# Revit family: Civil-Drainage-Channel-ACO-RoadDrain 200
name_source: partatom
category: Generic Models
revit_build: Autodesk Revit 2013 (Build: 20120221_2030(x64)
units: mm (PartAtom-declared; Revit-internal decimal feet)

## types (10) — shared parameters
Assembly Code = D2040
Fax = +44 (0)1462 815895
Installation guidelines = http://www.aco.co.uk
Maintenance guidelines = http://www.aco.co.uk
Manufacturer = ACO Technologies plc - ACO Water Management Division
Model = ACO RoadDrain 200 PD200F
Model Description = Monolithic Channel drainage system
Price = POA - contact ACO
Product Page URL = http://www.aco.co.uk
Product brochure = http://www.aco.co.uk
Revision = 1
SerialNumber = 0.000000
TagNumber = 0.000000
Telephone = +44 (0)1462 816666
URL = www.aco.co.uk
zero-valued in all types: Cost, Straight Void Start

## per-type parameters (varying)
- 33101 - PD200 F 10.1 Channel 500mm LG: ACO Hydraulic Design Software=http://www.acodesign.co.uk; Access unit=No; Channel 260mm Wide=Yes; Channel C.S.A=0.041m²; Channel Colour=Black; Channel Material=Vienite® Synthetic Resin Concrete; Channel Recyclable=Fully recyclable; Channel Recycled Material Content=20% minimum; Closing End Cap=No; Concrete Surround Volume - Load Class F 900 - Concrete Pavement=0.29m³/m; Hydraulic Performance=http://www.aco.co.uk; I/O End Cap Void=3000 mm  [stored 9.84252 ft]; Inlet Outlet end cap=No; Installation - Concrete Grade=Refer to brochure; Invert Depth=370mm; Invert Depth.=270 mm; Load Class=A 15 - F 900; Pipe Depth=6500 mm  [stored 21.3255 ft]; Product Code=33101; Product Dimensions=500mm x 260mm x 400mm (LxWxH); Product Standard=BS EN 1433:2002, CE marked, Kitemarked; Product Weight=52.0 Kg; Total Depth=400 mm  [stored 1.31234 ft]; Type Comments=ACO RoadDrain 200 PD200F 10.1 Constant Depth Channel 500mm Long; Void Depth=-400 mm  [stored -1.31234 ft]
- 33201 - PD200 F 20.1 Channel 500mm LG: ACO Hydraulic Design Software=http://www.acodesign.co.uk; Access unit=No; Channel 260mm Wide=Yes; Channel C.S.A=0.051m²; Channel Colour=Black; Channel Material=Vienite® Synthetic Resin Concrete; Channel Recyclable=Fully recyclable; Channel Recycled Material Content=20% minimum; Closing End Cap=No; Concrete Surround Volume - Load Class F 900 - Concrete Pavement=0.31m³/m; Hydraulic Performance=http://www.aco.co.uk; I/O End Cap Void=3005 mm  [stored 9.85892 ft]; Inlet Outlet end cap=No; Installation - Concrete Grade=Refer to brochure; Invert Depth=420mm; Invert Depth.=320 mm  [stored 1.04987 ft]; Load Class=A 15 - F 900; Pipe Depth=5400 mm  [stored 17.7165 ft]; Product Code=33201; Product Dimensions=500mm x 260mm x 450mm (LxWxH); Product Standard=BS EN 1433:2002, CE marked, Kitemarked; Product Weight=54.5 Kg; Total Depth=450 mm  [stored 1.47638 ft]; Type Comments=ACO RoadDrain 200 PD200F 20.1 Constant Depth Channel 500mm Long; Void Depth=-450 mm  [stored -1.47638 ft]
- 33301 - PD200 F 30.1 Channel 500mm LG: ACO Hydraulic Design Software=http://www.acodesign.co.uk; Access unit=No; Channel 260mm Wide=Yes; Channel C.S.A=0.061m²; Channel Colour=Black; Channel Material=Vienite® Synthetic Resin Concrete; Channel Recyclable=Fully recyclable; Channel Recycled Material Content=20% minimum; Closing End Cap=No; Concrete Surround Volume - Load Class F 900 - Concrete Pavement=0.33m³/m; Hydraulic Performance=http://www.aco.co.uk; I/O End Cap Void=3010 mm  [stored 9.87533 ft]; Inlet Outlet end cap=No; Installation - Concrete Grade=Refer to brochure; Invert Depth=470mm; Invert Depth.=370 mm  [stored 1.21391 ft]; Load Class=A 15 - F 900; Pipe Depth=5750 mm  [stored 18.8648 ft]; Product Code=33301; Product Dimensions=500mm x 260mm x 500mm (LxWxH); Product Standard=BS EN 1433:2002, CE marked, Kitemarked; Product Weight=58.3 Kg; Total Depth=500 mm  [stored 1.64042 ft]; Type Comments=ACO RoadDrain 100 PD200F 30.1 Constant Depth Channel 500mm Long; Void Depth=-500 mm  [stored -1.64042 ft]
- 33103 - PD 200 F 10.3 Rodding Access 500mm LG: ACO Hydraulic Design Software=http://www.acodesign.co.uk; Access Cover/Frame Colour=Black; Access Cover/Frame Finish=Water Based Paint Coating; Access Cover/Frame Material=Ductile Iron; Access Cover/Frame Recyclable=Fully recyclable; Access Cover/Frame Recycled Material Content=Between 40% - 90%; Access unit=Yes; Channel 260mm Wide=No; Channel C.S.A=0.41m²; Channel Colour=Black; Channel Material=Vienite® Synthetic Resin Concrete; Channel Recyclable=Fully recyclable; Channel Recycled Material Content=20% minimum; Closing End Cap=No; Concrete Surround Volume - Load Class F 900 - Concrete Pavement=0.29m³/m; Hydraulic Performance=http://www.aco.co.uk; I/O End Cap Void=3500 mm  [stored 11.4829 ft]; Inlet Outlet end cap=No; Installation - Concrete Grade=Refer to brochure; Invert Depth=370mm; Invert Depth.=270 mm; Load Class=A 15 - F 900; Pipe Depth=6000 mm  [stored 19.685 ft]; Product Code=33103; Product Dimensions=500mm x 260mm x 400mm (LxWxH); Product Standard=BS EN 1433:2002, CE marked, Kitemarked; Product Weight=53.5 Kg; Total Depth=400 mm  [stored 1.31234 ft]; Type Comments=ACO RoadDrain 200 PD200F 10.3 Constant Depth Access Channel 500mm Long; Void Depth=-400 mm  [stored -1.31234 ft]
- 33203 - PD200 F 20.3 Rodding Access 500mm LG: ACO Hydraulic Design Software=http://www.acodesign.co.uk; Access Cover/Frame Colour=Black; Access Cover/Frame Finish=Water Based Paint Coating; Access Cover/Frame Material=Ductile Iron; Access Cover/Frame Recyclable=Fully recyclable; Access Cover/Frame Recycled Material Content=Between 40% - 90%; Access unit=Yes; Channel 260mm Wide=No; Channel C.S.A=0.051m²; Channel Colour=Black; Channel Material=Vienite® Synthetic Resin Concrete; Channel Recyclable=Fully recyclable; Channel Recycled Material Content=20% minimum; Closing End Cap=No; Concrete Surround Volume - Load Class F 900 - Concrete Pavement=0.31m³/m; Hydraulic Performance=http://www.aco.co.uk; I/O End Cap Void=3260 mm  [stored 10.6955 ft]; Inlet Outlet end cap=No; Installation - Concrete Grade=Refer to brochure; Invert Depth=420mm; Invert Depth.=320 mm  [stored 1.04987 ft]; Load Class=A 15 - F 900; Pipe Depth=5800 mm  [stored 19.0289 ft]; Product Code=33203; Product Dimensions=500mm x 260mm x 450mm (LxWxH); Product Standard=BS EN 1433:2002, CE marked, Kitemarked; Product Weight=53.5 Kg; Total Depth=450 mm  [stored 1.47638 ft]; Type Comments=ACO RoadDrain 200 PD200F 20.3 Constant Depth Access Channel 500mm Long; Void Depth=-450 mm  [stored -1.47638 ft]
- 33306 - PD200 F 306 Closing endcap: Access unit=No; Channel 260mm Wide=No; Closing End Cap=Yes; End Cap Colour=Black; End Cap Material=Vienite® Synthetic Resin Concrete; End Cap Recyclable=Fully recyclable; End Cap Recycled Material Content=20% minimum; I/O End Cap Void=3650 mm  [stored 11.9751 ft]; Inlet Outlet end cap=No; Invert Depth.=275 mm; Pipe Depth=3000 mm  [stored 9.84252 ft]; Product Code=33306; Product Dimensions=25mm x 260mm x 500mm (LxWxH); Product Weight=4.6 Kg; Total Depth=500 mm  [stored 1.64042 ft]; Type Comments=ACO RoadDrain PD200 F 306 Closing End Cap; Void Depth=-500 mm  [stored -1.64042 ft]
- 33108 - PD200 F 108 Inlet/outlet endcap: Access unit=No; Channel 260mm Wide=No; Closing End Cap=No; Connection Pipe Colour=Brown; Connection Pipe Material=PVCu; Connection Pipe O.D=Ø160mm; End Cap Colour=Black; End Cap Material=Vienite® Synthetic Resin Concrete; End Cap Recyclable=Fully recyclable; End Cap Recycled Material Content=20% minimum; I/O End Cap Void=128 mm; Inlet Outlet end cap=Yes; Invert Depth.=270 mm; Pipe Depth=299 mm; Product Code=33108; Product Dimensions=25mm x 260mm x 400mm (LxWxH); Product Weight=4.3 Kg; Total Depth=400 mm  [stored 1.31234 ft]; Type Comments=ACO RoadDrain PD200 F 108 Inlet/Outlet End Cap; Void Depth=-400 mm  [stored -1.31234 ft]
- 33208 - PD200 F 208 Inlet/outlet endcap: Access unit=No; Channel 260mm Wide=No; Closing End Cap=No; Connection Pipe Colour=Brown; Connection Pipe Material=PVCu; Connection Pipe O.D=Ø160mm; End Cap Colour=Black; End Cap Material=Vienite® Synthetic Resin Concrete; End Cap Recyclable=Fully recyclable; End Cap Recycled Material Content=20% minimum; I/O End Cap Void=228 mm  [stored 0.748031 ft]; Inlet Outlet end cap=Yes; Invert Depth.=275 mm; Pipe Depth=349 mm; Product Code=33208; Product Dimensions=25mm x 260mm x 450mm (LxWxH); Product Weight=4.7 Kg; Total Depth=450 mm  [stored 1.47638 ft]; Type Comments=ACO RoadDrain PD200 F 208 Inlet/Outlet End Cap; Void Depth=-450 mm  [stored -1.47638 ft]
- 33303 - PD 200 F 30.3 Rodding Access 500mm LG: ACO Hydraulic Design Software=http://www.acodesign.co.uk; Access Cover/Frame Colour=Black; Access Cover/Frame Finish=Water Based Paint Coating; Access Cover/Frame Material=Ductile Iron; Access Cover/Frame Recyclable=Fully recyclable; Access Cover/Frame Recycled Material Content=Between 40% - 90%; Access unit=Yes; Channel 260mm Wide=No; Channel C.S.A=0.061m²; Channel Colour=Black; Channel Material=Vienite® Synthetic Resin Concrete; Channel Recyclable=Fully recyclable; Channel Recycled Material Content=20% minimum; Closing End Cap=No; Concrete Surround Volume - Load Class F 900 - Concrete Pavement=0.33m³/m; Hydraulic Performance=http://www.aco.co.uk; I/O End Cap Void=3500 mm  [stored 11.4829 ft]; Inlet Outlet end cap=No; Installation - Concrete Grade=Refer to brochure; Invert Depth=470mm; Invert Depth.=370 mm  [stored 1.21391 ft]; Load Class=A 15 - F 900; Pipe Depth=5650 mm  [stored 18.5367 ft]; Product Code=33303; Product Dimensions=500mm x 260mm x 500mm (LxWxH); Product Standard=BS EN 1433:2002, CE marked, Kitemarked; Product Weight=66.0 Kg; Total Depth=500 mm  [stored 1.64042 ft]; Type Comments=ACO RoadDrain 200 PD200F 30.3 Constant Depth Access Channel 500mm Long; Void Depth=-500 mm  [stored -1.64042 ft]
- 33308 - PD200 F 308 Inlet/outlet endcap: Access unit=No; Channel 260mm Wide=No; Closing End Cap=No; Connection Pipe Colour=Brown; Connection Pipe Material=PVCu; Connection Pipe O.D=Ø160mm; End Cap Colour=Black; End Cap Material=Vienite® Synthetic Resin Concrete; End Cap Recyclable=Fully recyclable; End Cap Recycled Material Content=20% minimum; I/O End Cap Void=228 mm  [stored 0.748031 ft]; Inlet Outlet end cap=Yes; Invert Depth.=325 mm  [stored 1.06627 ft]; Pipe Depth=399 mm; Product Code=33308; Product Dimensions=25mm x 260mm x 500mm (LxWxH); Product Weight=5.2 kg; Total Depth=500 mm  [stored 1.64042 ft]; Type Comments=ACO RoadDrain PD200 F 308 Inlet/Outlet End Cap; Void Depth=-500 mm  [stored -1.64042 ft]

note: [stored X ft] marks values corroborated as IEEE doubles in the binary element streams (Revit-internal decimal feet)

## geometry (parser evidence)
native form markers: Blend x6, Sweep x1
no freeform markers — native parametric forms only
